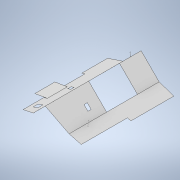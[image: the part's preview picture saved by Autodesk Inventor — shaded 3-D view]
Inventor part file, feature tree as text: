
AUTODESK INVENTOR PART (.ipt)
format: ipt  version: 2022.1 (Build 261234000, 234)  size: 240,128 bytes
history: native  units: in
note: dims shown in document units (in); Inventor stores cm internally (conversion verified against a paired STEP export)
features: sketch x7, extrude x7, plane x6
ambient origin geometry x8: Origin, YZ Plane, XZ Plane, XY Plane, X Axis, Y Axis, Z Axis, Center Point
bodies: Body1 (feature_tree)
feature tree (20):
  plane  "Work Plane3"
  sketch  "Sketch8"  dims[d38=45.0deg d39=690.0in]
  plane  "Work Plane5"
  sketch  "Sketch9"  dims[d40=185.0in d41=157.0in]
  plane  "Work Plane6"
  sketch  "Sketch11"  dims[d42=223.0in d49=0.1267in]
  plane  "Work Plane8"
  sketch  "Sketch13"  dims[d50=117.0in d51=187.0in]
  extrude  "Extrusion12"  Depth=690.0in
  extrude  "Extrusion13"  Depth=157.0in
  extrude  "Extrusion15"  Depth=223.0in
  plane  "Work Plane9"
  extrude  "Extrusion16"  Depth=187.0in
  extrude  "Extrusion17"  Depth=25.0in
  plane  "Work Plane10"
  extrude  "Extrusion18"  Depth=144.0in
  extrude  "Extrusion19"  Depth=690.0in
  sketch  "Sketch14"  dims[d52=25.0in d59=654.0287in]
  sketch  "Sketch15"  dims[d60=149.0in d61=144.0in]
  sketch  "Sketch16"  dims[d62=-0.3092in d63=690.0in d65=183.0in d66=648.0in d67=0.5296in d74=156.0in d75=222.0in d76=-0.1267in d77=112.0in d78=310.0in d79=25.0in d80=333.0in d81=24.0in d84=35.5in d85=36.0in d86=37.0in d87=35.25in d90=165.17in d91=0.001in d92=0.0in d93=0.001in d94=0.0in d97=0.001in d98=0.0in d103=17.0in d104=31.0in d105=31.0in d106=65.0in d107=0.065in d108=91.0in d109=0.001in d110=0.0in d111=48.0in d112=35.9103in d115=8.2in d116=23.0in d117=40.0in d118=75.0in d119=0.001in d120=0.0in d121=2.0in d122=36.0in d123=0.0in d124=2.0in d125=36.0in d126=0.0in d127=87.0in d95=0.5in d96=0.0344in]
